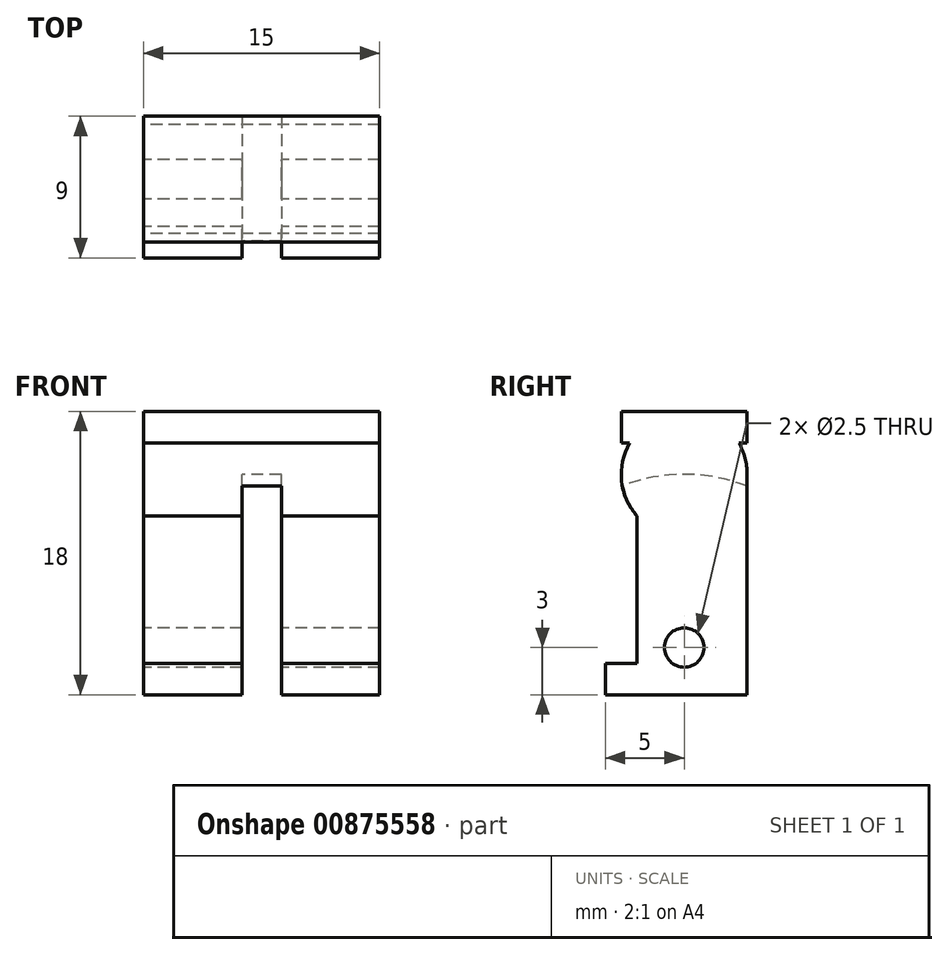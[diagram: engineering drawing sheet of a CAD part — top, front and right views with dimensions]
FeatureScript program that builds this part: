
annotation { "Feature Type Name" : "Feature", "Feature Type Description" : "" }
export const myFeature = defineFeature(function(context is Context, id is Id, definition is map)
    precondition{}
    {
        {
            var Q0;
            Q0=qCreatedBy(makeId("Right.planeOp"),FACE);
            var sketch = newSketch(context, id + "F0", { "sketchPlane" : qUnion([Q0])});
            skLineSegment(sketch, "E0.bottom", {"start": v(4, -1) * mm, "end": v(3.46, -1) * mm});
            skLineSegment(sketch, "E0.top", {"start": v(4, 1) * mm, "end": v(-4, 1) * mm});
            skLineSegment(sketch, "E0.left", {"start": v(4, -1) * mm, "end": v(4, 1) * mm});
            skLineSegment(sketch, "E0.right", {"start": v(-4, -1) * mm, "end": v(-4, 1) * mm});
            skPoint(sketch, "E0.middle", {"position": v(0, 0) * mm});
            skArc(sketch, "E1", {"start": v(4, -3) * mm, "mid": v(3.86, -1.96) * mm, "end": v(3.46, -1) * mm});
            skPoint(sketch, "E1.centerSnap0", {"position": v(0, -1) * mm});
            skLineSegment(sketch, "E2.left", {"start": v(4, -3) * mm, "end": v(4, -15) * mm});
            skLineSegment(sketch, "E2.right", {"start": v(-3, -5.65) * mm, "end": v(-3, -15) * mm});
            skLineSegment(sketch, "E3.bottom", {"start": v(-3, -15) * mm, "end": v(-5, -15) * mm});
            skLineSegment(sketch, "E3.top", {"start": v(4, -17) * mm, "end": v(-5, -17) * mm});
            skLineSegment(sketch, "E3.left", {"start": v(4, -15) * mm, "end": v(4, -17) * mm});
            skLineSegment(sketch, "E3.right", {"start": v(-5, -15) * mm, "end": v(-5, -17) * mm});
            skCircle(sketch, "E4", {"center": v(0, -14) * mm, "radius": 1.25 * mm});
            skLineSegment(sketch, "E5.trimOffspring", {"start": v(-3.46, -1) * mm, "end": v(-4, -1) * mm});
            skArc(sketch, "E6.trimOffspring", {"start": v(-3.46, -1) * mm, "mid": v(-3.98, -3.4) * mm, "end": v(-3, -5.65) * mm});
            skSolve(sketch);
        }
        {
            var Q0;
            Q0 = qSketchRegion(id + "F0", true);
            extrude(context, id + "F1", {"entities" : qUnion([Q0]), "endBound" : BoundingType.SYMMETRIC, "depth" : 15 * mm, "offsetDistance" : 25 * mm});
        }
        {
            var Q0;
            Q0=qCreatedBy(makeId("Right.planeOp"),FACE);
            var sketch = newSketch(context, id + "F2", { "sketchPlane" : qUnion([Q0])});
            skCircle(sketch, "E7", {"center": v(0, -14) * mm, "radius": 11 * mm});
            skSolve(sketch);
        }
        {
            var Q0;
            Q0=makeQuery(id+"F2.imprint","IMPRINT",FACE,{"disambiguationData":[TD([[makeQuery(id+"F2.imprint","IMPRINT",EDGE,{"derivedFrom":sQuery(id+"F2.wireOp",EDGE,"E7")}),1.0]])]});
            var Q1;
            Q1=sQuery(id+"F2.wireOp",EDGE,"E7");
            extrude(context, id + "F3", {"entities" : qUnion([Q0]), "operationType" : NewBodyOperationType.REMOVE, "surfaceEntities" : qUnion([Q1]), "endBound" : BoundingType.SYMMETRIC, "depth" : 2.5 * mm, "offsetDistance" : 25 * mm});
        }
    });
